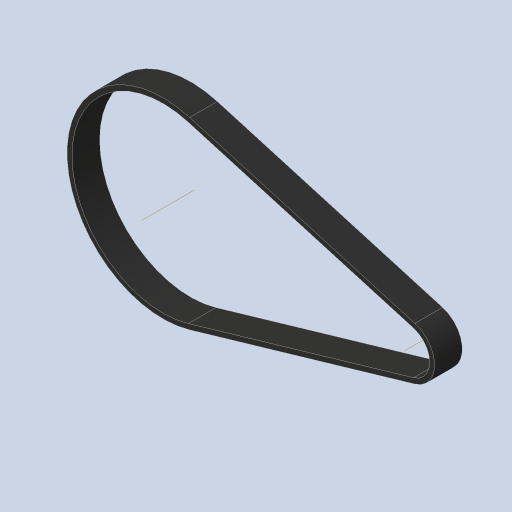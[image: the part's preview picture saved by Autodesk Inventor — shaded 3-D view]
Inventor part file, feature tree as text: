
AUTODESK INVENTOR PART (.ipt)
format: ipt  version: 2023.4 (Build 274418000, 418)  size: 172,544 bytes
history: native  units: in
note: dims shown in document units (in); Inventor stores cm internally (conversion verified against a paired STEP export)
features: sketch x3, extrude x1, other x1, projected_geometry x1
ambient origin geometry x8: Origin, YZ Plane, XZ Plane, XY Plane, X Axis, Y Axis, Z Axis, Center Point
bodies: Body1 (feature_tree)
feature tree (6):
  sketch  "Sketch2"  dims[d0=0.6015in d1=2.2558in]
  extrude  "Extrusion2"  Depth=2.2558in
  sketch  "Sketch5"  dims[d3=4.1836in d5=2.8361in d9=0.0787in d10=0.0598in d11=0.0299in d12=0.0219in d13=0.0219in d14=0.0059in d15=0.0059in d20=0.3346in d21=0.0in d22=0.0787in d23=0.0598in d24=0.0299in d25=0.0219in d26=0.0219in d27=0.0059in d28=0.0059in d29=0.0299in d30=0.0394in d31=0.0787in d32=0.0232in d34=0.0219in d35=0.0in d36=0.0in d37=0.0059in d38=0.0022in d39=0.0022in d40=0.0in d41=0.0in d42=0.0081in d43=0.0081in d44=0.0299in]
  other  "Work Axis1"
  sketch  "Sketch4"  dims[d2=0.7742in]
  projected_geometry  "Projected Loop1"
